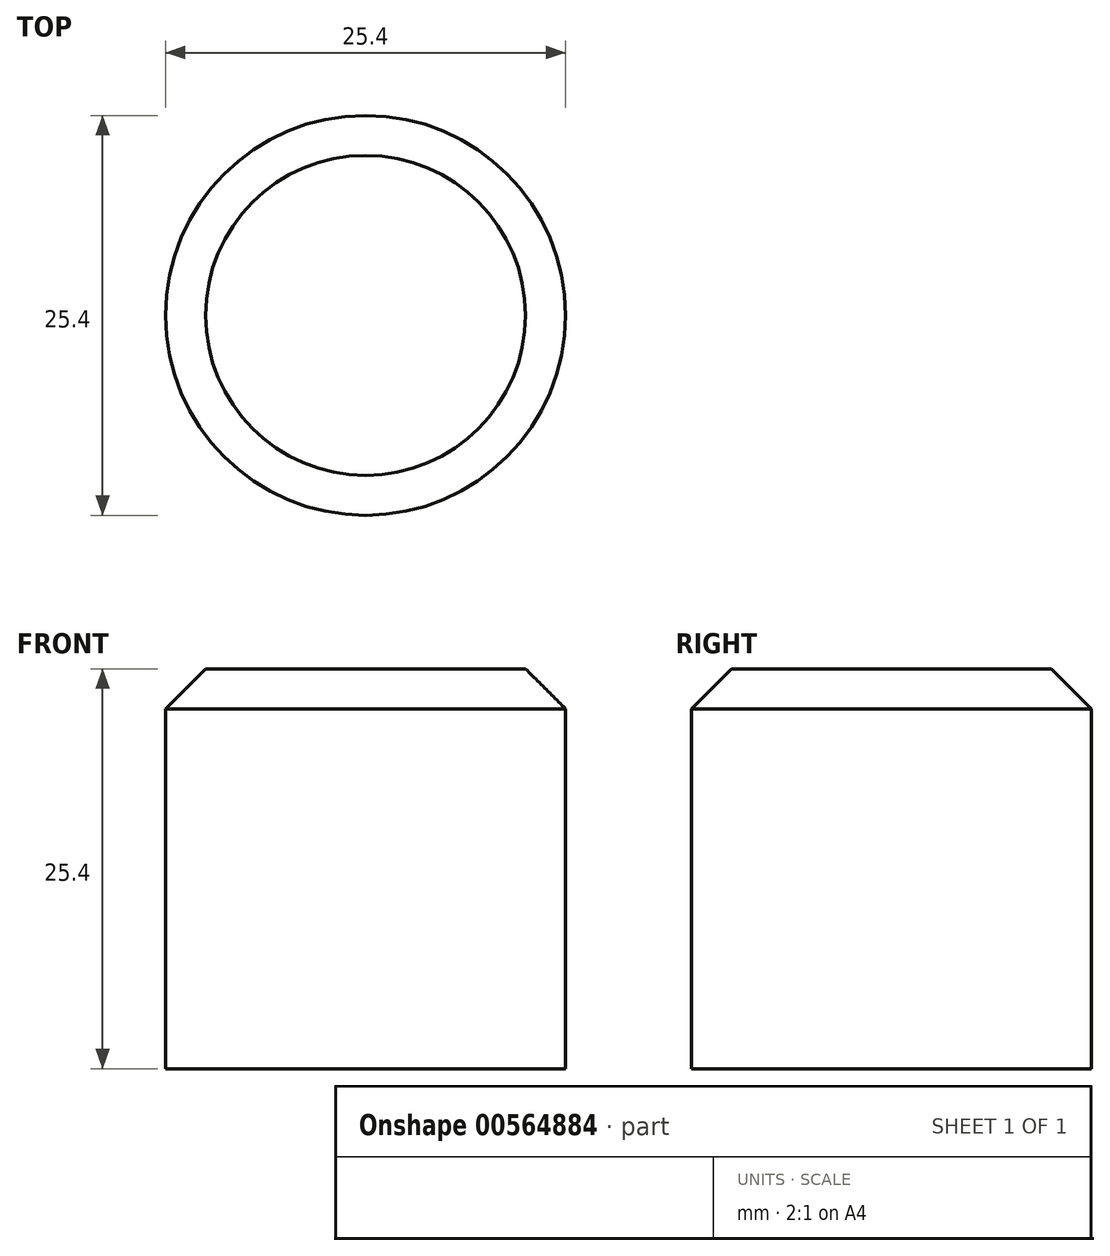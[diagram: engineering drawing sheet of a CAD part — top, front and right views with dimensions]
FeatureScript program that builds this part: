
annotation { "Feature Type Name" : "Feature", "Feature Type Description" : "" }
export const myFeature = defineFeature(function(context is Context, id is Id, definition is map)
    precondition{}
    {
        {
            var Q0;
            Q0=qCreatedBy(makeId("Top.planeOp"),FACE);
            var sketch = newSketch(context, id + "F0", { "sketchPlane" : qUnion([Q0])});
            skCircle(sketch, "E0", {"center": v(0, 0) * mm, "radius": 12.7 * mm});
            skSolve(sketch);
        }
        {
            var Q0;
            Q0=makeQuery(id+"F0.imprint","IMPRINT",FACE,{"disambiguationData":[TD([[makeQuery(id+"F0.imprint","IMPRINT",EDGE,{"derivedFrom":sQuery(id+"F0.wireOp",EDGE,"E0")}),1.0]])]});
            extrude(context, id + "F1", {"entities" : qUnion([Q0]), "depth" : 25.4 * mm, "offsetDistance" : 25.4 * mm});
        }
        {
            var Q0;
            Q0=makeQuery(id+"F1.opExtrude","CAP_EDGE",EDGE,{"disambiguationData":[OSD([sQuery(id+"F0.wireOp",EDGE,"E0")])],"isStart":false});
            chamfer(context, id + "F2", {"entities" : qUnion([Q0]), "chamferType" : ChamferType.OFFSET_ANGLE, "width" : 2.54 * mm, "oppositeDirection" : false, "angle" : 45 * degree, "tangentPropagation" : true});
        }
    });
